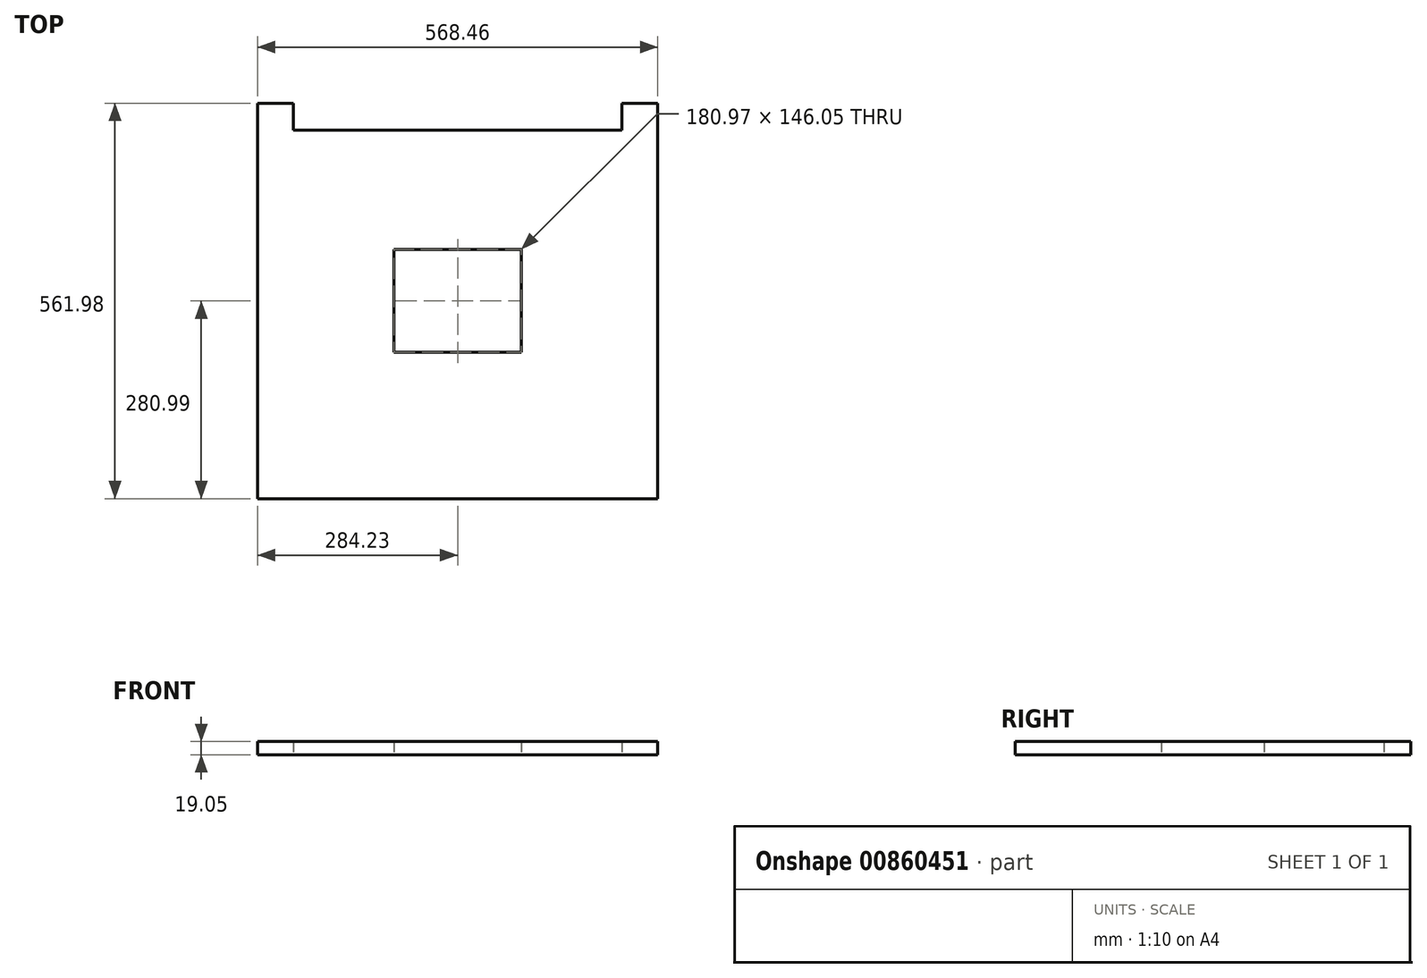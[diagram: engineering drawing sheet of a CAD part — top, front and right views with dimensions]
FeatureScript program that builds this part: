
annotation { "Feature Type Name" : "Feature", "Feature Type Description" : "" }
export const myFeature = defineFeature(function(context is Context, id is Id, definition is map)
    precondition{}
    {
        {
            var Q0;
            Q0=qCreatedBy(makeId("Top.planeOp"),FACE);
            var sketch = newSketch(context, id + "F0", { "sketchPlane" : qUnion([Q0])});
            skLineSegment(sketch, "E0.bottom", {"start": v(284.23, 280.99) * mm, "end": v(-284.23, 280.99) * mm});
            skLineSegment(sketch, "E0.top", {"start": v(284.23, -280.99) * mm, "end": v(-284.23, -280.99) * mm});
            skLineSegment(sketch, "E0.left", {"start": v(284.23, 280.99) * mm, "end": v(284.23, -280.99) * mm});
            skLineSegment(sketch, "E0.right", {"start": v(-284.23, 280.99) * mm, "end": v(-284.23, -280.99) * mm});
            skPoint(sketch, "E0.middle", {"position": v(0, 0) * mm});
            skLineSegment(sketch, "E1", {"start": v(-284.23, 280.99) * mm, "end": v(-233.43, 280.99) * mm});
            skLineSegment(sketch, "E2", {"start": v(284.23, 280.99) * mm, "end": v(233.43, 280.99) * mm});
            skLineSegment(sketch, "E3", {"start": v(-233.43, 280.99) * mm, "end": v(-233.43, 242.89) * mm});
            skLineSegment(sketch, "E4", {"start": v(-233.43, 242.89) * mm, "end": v(233.43, 242.89) * mm});
            skLineSegment(sketch, "E5", {"start": v(233.43, 242.89) * mm, "end": v(233.43, 280.99) * mm});
            skLineSegment(sketch, "E6.bottom", {"start": v(90.49, 73.03) * mm, "end": v(-90.49, 73.03) * mm});
            skLineSegment(sketch, "E6.top", {"start": v(90.49, -73.02) * mm, "end": v(-90.49, -73.03) * mm});
            skLineSegment(sketch, "E6.left", {"start": v(90.49, 73.03) * mm, "end": v(90.49, -73.02) * mm});
            skLineSegment(sketch, "E6.right", {"start": v(-90.49, 73.03) * mm, "end": v(-90.49, -73.03) * mm});
            skSolve(sketch);
        }
        {
            var Q0;
            Q0=makeQuery(id+"F0.imprint","IMPRINT",FACE,{"disambiguationData":[TD([[makeQuery(id+"F0.imprint","IMPRINT",EDGE,{"derivedFrom":sQuery(id+"F0.wireOp",EDGE,"E0.top")}),-1.0]])]});
            extrude(context, id + "F1", {"entities" : qUnion([Q0]), "depth" : 19.05 * mm, "offsetDistance" : 25.4 * mm});
        }
    });
